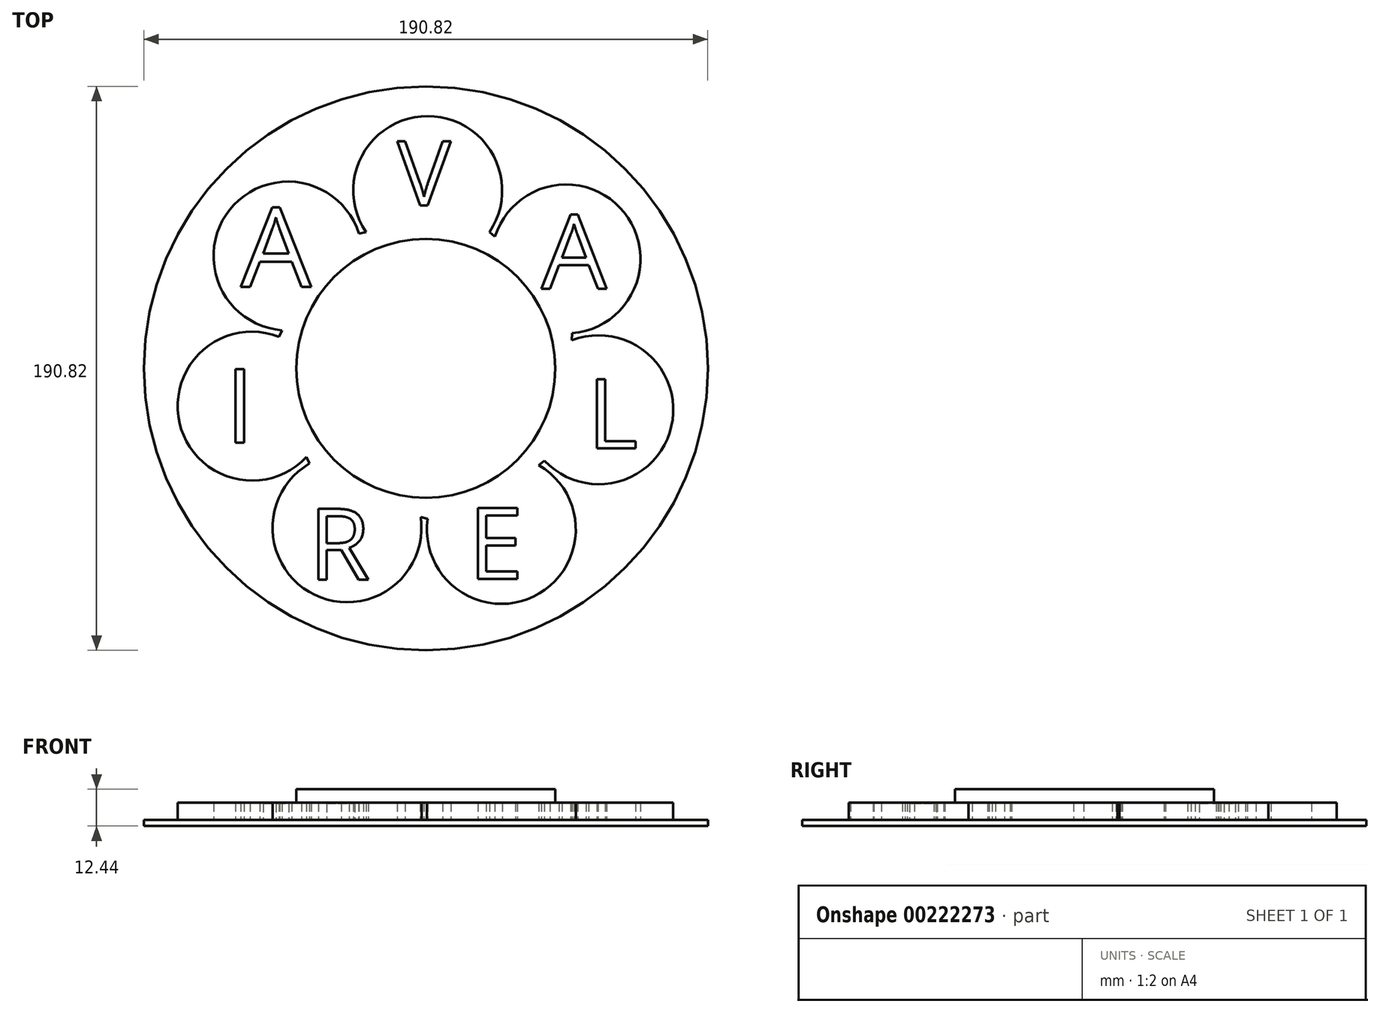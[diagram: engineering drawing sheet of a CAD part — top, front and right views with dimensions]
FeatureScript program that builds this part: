
annotation { "Feature Type Name" : "Feature", "Feature Type Description" : "" }
export const myFeature = defineFeature(function(context is Context, id is Id, definition is map)
    precondition{}
    {
        {
            var Q0;
            Q0=qCreatedBy(makeId("Top.planeOp"),FACE);
            var sketch = newSketch(context, id + "F0", { "sketchPlane" : qUnion([Q0])});
            skCircle(sketch, "E0", {"center": v(0, 0) * mm, "radius": 43.8 * mm});
            skArc(sketch, "E1", {"start": v(21.52, 46.08) * mm, "mid": v(0.63, 85.36) * mm, "end": v(-20.26, 46.08) * mm});
            skArc(sketch, "E2.1.0", {"start": v(-22.6, 45.56) * mm, "mid": v(-66.34, 53.72) * mm, "end": v(-48.66, 12.9) * mm});
            skArc(sketch, "E2.2.0", {"start": v(-49.72, 10.73) * mm, "mid": v(-83.36, -18.38) * mm, "end": v(-40.42, -30) * mm});
            skArc(sketch, "E2.3.0", {"start": v(-39.38, -32.18) * mm, "mid": v(-37.6, -76.63) * mm, "end": v(-1.74, -50.3) * mm});
            skArc(sketch, "E2.4.0", {"start": v(0.6, -50.86) * mm, "mid": v(36.47, -77.18) * mm, "end": v(38.24, -32.73) * mm});
            skArc(sketch, "E2.5.0", {"start": v(40.14, -31.24) * mm, "mid": v(83.08, -19.61) * mm, "end": v(49.43, 9.5) * mm});
            skArc(sketch, "E2.6.0", {"start": v(49.45, 11.9) * mm, "mid": v(67.13, 52.73) * mm, "end": v(23.4, 44.57) * mm});
            skLineSegment(sketch, "E3", {"start": v(-22.6, 45.56) * mm, "end": v(-20.26, 46.08) * mm});
            skLineSegment(sketch, "E4", {"start": v(-48.66, 12.9) * mm, "end": v(-49.72, 10.73) * mm});
            skLineSegment(sketch, "E5", {"start": v(-40.42, -30) * mm, "end": v(-39.38, -32.18) * mm});
            skLineSegment(sketch, "E6", {"start": v(-1.74, -50.3) * mm, "end": v(0.6, -50.86) * mm});
            skLineSegment(sketch, "E7", {"start": v(40.14, -31.24) * mm, "end": v(38.24, -32.73) * mm});
            skLineSegment(sketch, "E8", {"start": v(49.45, 11.9) * mm, "end": v(49.43, 9.5) * mm});
            skLineSegment(sketch, "E9", {"start": v(21.52, 46.08) * mm, "end": v(23.4, 44.57) * mm});
            skText(sketch, "E10", { "text": "V", "fontName": "OpenSans-Regular.ttf"});
            skText(sketch, "E11", { "text": "A", "fontName": "OpenSans-Regular.ttf"});
            skText(sketch, "E12", { "text": "L", "fontName": "OpenSans-Regular.ttf"});
            skText(sketch, "E13", { "text": "E", "fontName": "OpenSans-Regular.ttf"});
            skText(sketch, "E14", { "text": "R", "fontName": "OpenSans-Regular.ttf"});
            skText(sketch, "E15", { "text": "I", "fontName": "OpenSans-Regular.ttf"});
            skText(sketch, "E16", { "text": "A", "fontName": "OpenSans-Regular.ttf"});
            const initialGuessF0  = {"E10": [-0.00968, 0.05513, 1, 0, 0.02195], "E11": [0.03906, 0.02697, 1, 0, 0.02522], "E12": [0.0547, -0.02704, 1, 0, 0.02358], "E13": [0.01439, -0.07119, 1, 0, 0.02413], "E14": [-0.03963, -0.07146, 1, 0, 0.02413], "E15": [-0.06787, -0.02512, 1, 0, 0.02512], "E16": [-0.06266, 0.02752, 1, 0, 0.02714]};
            skSetInitialGuess(sketch, initialGuessF0);
            skSolve(sketch);
        }
        {
            var Q0;
            Q0=makeQuery(id+"F0.imprint","IMPRINT",FACE,{"disambiguationData":[TD([[makeQuery(id+"F0.imprint","IMPRINT",EDGE,{"derivedFrom":sQuery(id+"F0.wireOp",EDGE,"E0")}),1.0]])]});
            extrude(context, id + "F1", {"entities" : qUnion([Q0]), "depth" : 10.4 * mm});
        }
        {
            var Q0;
            Q0=makeQuery(id+"F0.imprint","IMPRINT",FACE,{"disambiguationData":[TD([[makeQuery(id+"F0.imprint","IMPRINT",EDGE,{"derivedFrom":sQuery(id+"F0.wireOp",EDGE,"E0")}),-1.0]])]});
            var Q1;
            Q1=makeQuery(id+"F0.imprint","IMPRINT",FACE,{"disambiguationData":[TD([[makeQuery(id+"F0.imprint","IMPRINT",EDGE,{"derivedFrom":sQuery(id+"F0.wireOp",EDGE,"E11.sketch_text.stroke-8")}),1.0]])]});
            extrude(context, id + "F2", {"entities" : qUnion([Q0, Q1]), "operationType" : NewBodyOperationType.ADD, "depth" : 5.84 * mm});
        }
        {
            var Q0;
            Q0=makeQuery(id+"F0.imprint","IMPRINT",FACE,{"disambiguationData":[TD([[makeQuery(id+"F0.imprint","IMPRINT",EDGE,{"derivedFrom":sQuery(id+"F0.wireOp",EDGE,"E14.sketch_text.stroke-11")}),1.0]])]});
            var Q1;
            Q1=makeQuery(id+"F0.imprint","IMPRINT",FACE,{"disambiguationData":[TD([[makeQuery(id+"F0.imprint","IMPRINT",EDGE,{"derivedFrom":sQuery(id+"F0.wireOp",EDGE,"E16.sketch_text.stroke-8")}),1.0]])]});
            extrude(context, id + "F3", {"entities" : qUnion([Q0, Q1]), "depth" : 5.6 * mm});
        }
        {
            var Q0;
            Q0=qCreatedBy(makeId("Top.planeOp"),FACE);
            var sketch = newSketch(context, id + "F4", { "sketchPlane" : qUnion([Q0])});
            skCircle(sketch, "E17", {"center": v(0, 0) * mm, "radius": 95.41 * mm});
            skSolve(sketch);
        }
        {
            var Q0;
            Q0=makeQuery(id+"F4.imprint","IMPRINT",FACE,{"disambiguationData":[TD([[makeQuery(id+"F4.imprint","IMPRINT",EDGE,{"derivedFrom":sQuery(id+"F4.wireOp",EDGE,"E17")}),1.0]])]});
            extrude(context, id + "F5", {"entities" : qUnion([Q0]), "oppositeDirection" : true, "depth" : 2.03 * mm});
        }
    });
